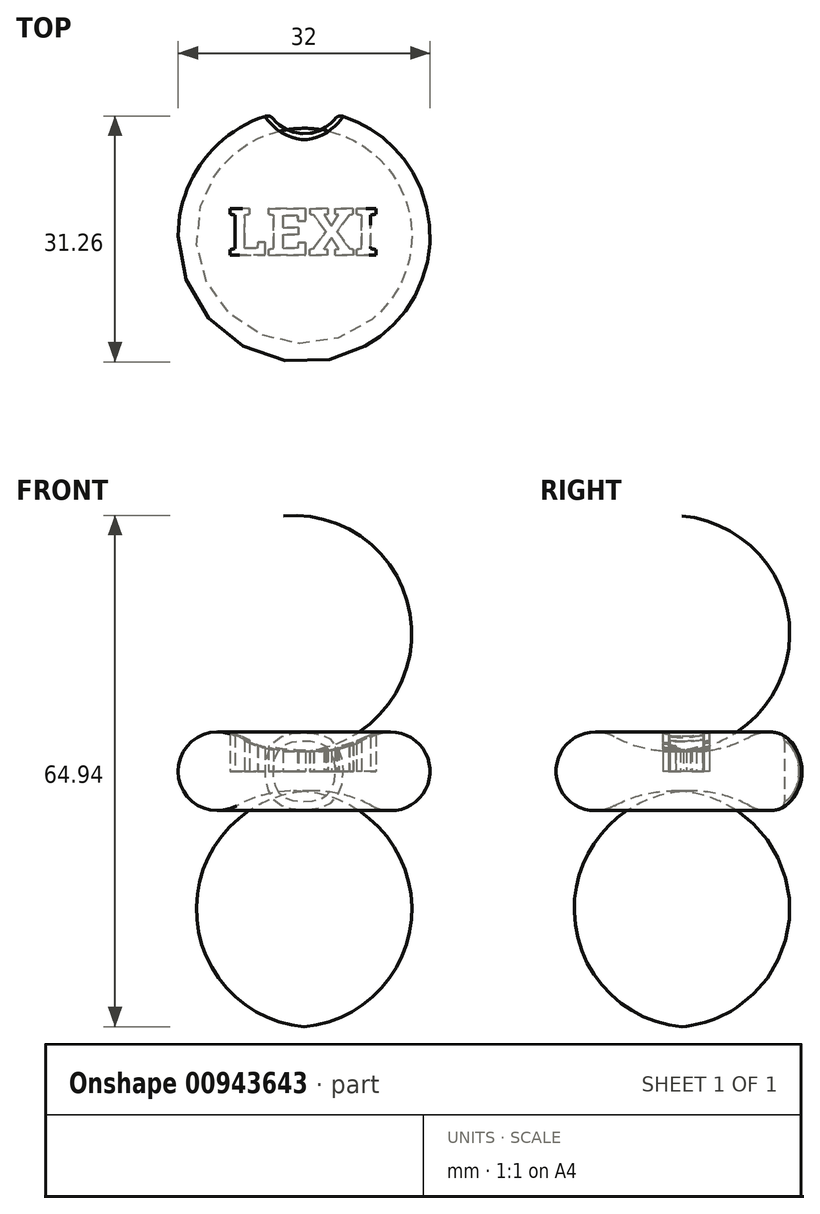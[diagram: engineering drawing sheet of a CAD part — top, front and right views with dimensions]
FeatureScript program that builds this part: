
annotation { "Feature Type Name" : "Feature", "Feature Type Description" : "" }
export const myFeature = defineFeature(function(context is Context, id is Id, definition is map)
    precondition{}
    {
        {
            var Q0;
            Q0=qCreatedBy(makeId("Front.planeOp"),FACE);
            var sketch = newSketch(context, id + "F0", { "sketchPlane" : qUnion([Q0])});
            skArc(sketch, "E0", {"start": v(0, -2.56) * mm, "mid": v(-4.43, -2.83) * mm, "end": v(-8.58, -4.38) * mm});
            skArc(sketch, "E1", {"start": v(-8.58, 4.38) * mm, "mid": v(-16, 0) * mm, "end": v(-8.58, -4.38) * mm});
            skArc(sketch, "E2", {"start": v(-8.58, 4.38) * mm, "mid": v(-4.43, 2.83) * mm, "end": v(0, 2.56) * mm});
            skLineSegment(sketch, "E3", {"start": v(0, -2.56) * mm, "end": v(0, 2.56) * mm});
            skSolve(sketch);
        }
        {
            var Q0;
            Q0=makeQuery(id+"F0.imprint","IMPRINT",FACE,{"disambiguationData":[TD([[makeQuery(id+"F0.imprint","IMPRINT",EDGE,{"derivedFrom":sQuery(id+"F0.wireOp",EDGE,"E0")}),-1.0]])]});
            var Q1;
            Q1=sQuery(id+"F0.wireOp",EDGE,"E3");
            revolve(context, id + "F1", {"surfaceOperationType" : NewSurfaceOperationType.NEW, "entities" : qUnion([Q0]), "axis" : qUnion([Q1]), "revolveType" : RevolveType.FULL});
        }
        {
            var Q0;
            Q0=qCreatedBy(makeId("Top.planeOp"),FACE);
            var sketch = newSketch(context, id + "F2", { "sketchPlane" : qUnion([Q0])});
            skCircle(sketch, "E4", {"center": v(0, 18) * mm, "radius": 5 * mm});
            skSolve(sketch);
        }
        {
            var Q0;
            Q0 = qSketchRegion(id + "F2", true);
            extrude(context, id + "F3", {"entities" : qUnion([Q0]), "operationType" : NewBodyOperationType.REMOVE, "endBound" : BoundingType.SYMMETRIC, "depth" : 25 * mm, "offsetDistance" : 25 * mm});
        }
        {
            var Q0;
            Q0=makeQuery(id+"F3.boolean.opBoolean","COPY",FACE,{"derivedFrom":makeQuery(id+"F3.opExtrude","SWEPT_FACE",FACE,{"disambiguationData":[OSD([sQuery(id+"F2.wireOp",EDGE,"E4")])]})});
            fillet(context, id + "F4", {"entities" : qUnion([Q0]), "radius" : 1 * mm, "tangentPropagation" : true, "rho" : 0.5, "crossSection" : FilletCrossSection.CONIC, "allowEdgeOverflow" : false});
        }
        {
            var Q0;
            Q0=qCreatedBy(makeId("Top.planeOp"),FACE);
            var sketch = newSketch(context, id + "F5", { "sketchPlane" : qUnion([Q0])});
            skText(sketch, "E5", { "text": "LEXI", "fontName": "RobotoSlab-Bold.ttf"});
            const initialGuessF5  = {"E5": [-0.00963, -0.00243, 1, 0, 0.006]};
            skSetInitialGuess(sketch, initialGuessF5);
            skSolve(sketch);
        }
        {
            var Q0;
            Q0 = qSketchRegion(id + "F5", true);
            extrude(context, id + "F6", {"entities" : qUnion([Q0]), "operationType" : NewBodyOperationType.REMOVE, "depth" : 25 * mm, "offsetDistance" : 25 * mm});
        }
    });
